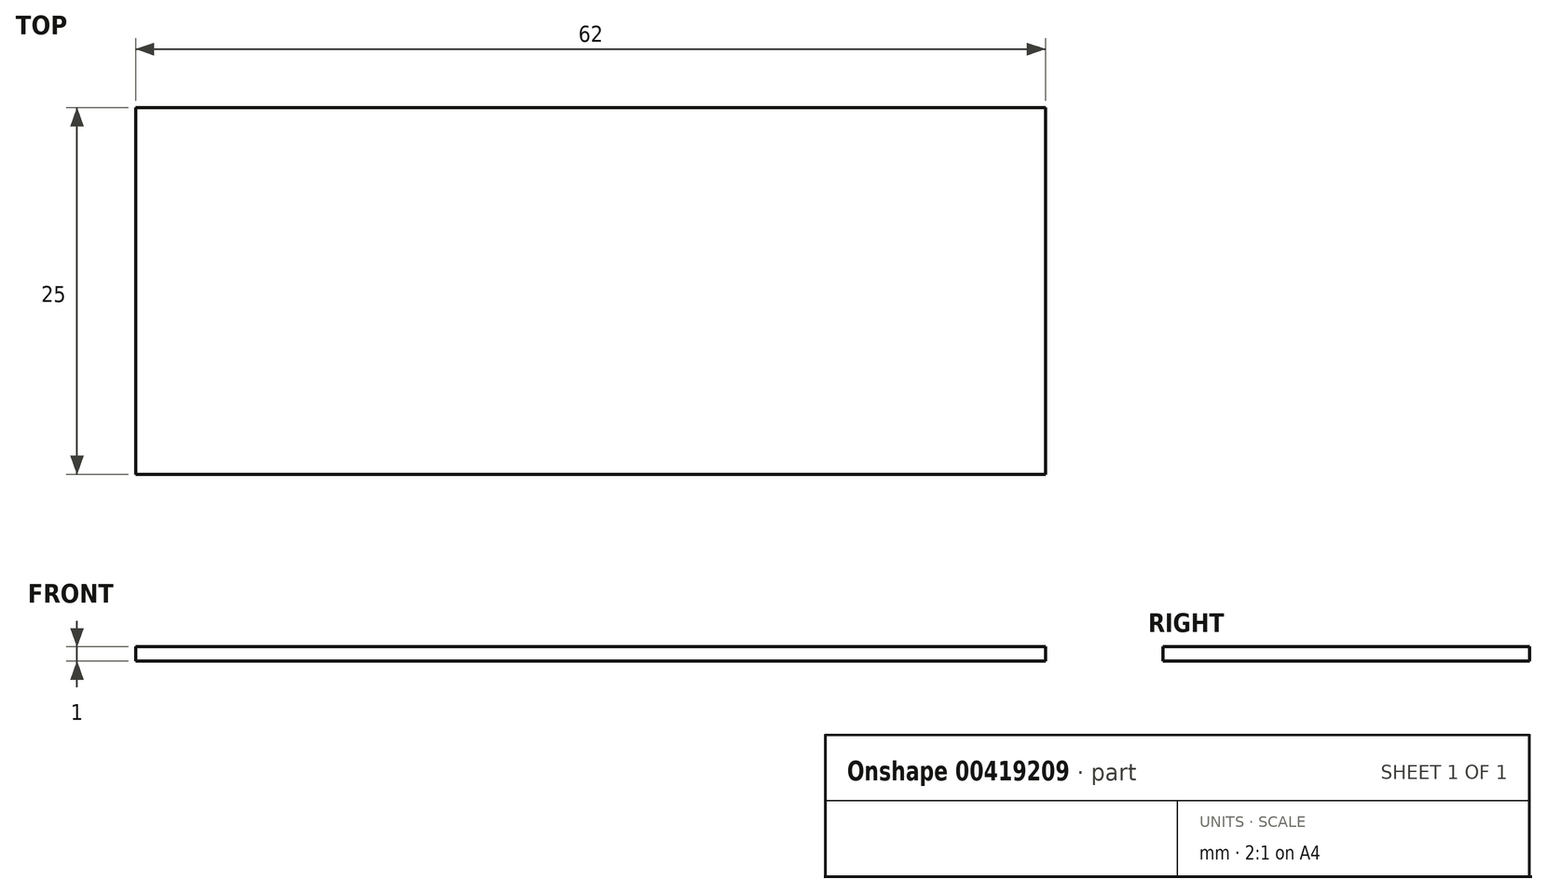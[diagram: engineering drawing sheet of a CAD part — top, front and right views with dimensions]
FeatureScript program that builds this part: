
annotation { "Feature Type Name" : "Feature", "Feature Type Description" : "" }
export const myFeature = defineFeature(function(context is Context, id is Id, definition is map)
    precondition{}
    {
        {
            var Q0;
            Q0=qCreatedBy(makeId("Top.planeOp"),FACE);
            var sketch = newSketch(context, id + "F0", { "sketchPlane" : qUnion([Q0])});
            skLineSegment(sketch, "E0.bottom", {"start": v(31, 12.5) * mm, "end": v(-31, 12.5) * mm});
            skLineSegment(sketch, "E0.top", {"start": v(31, -12.5) * mm, "end": v(-31, -12.5) * mm});
            skLineSegment(sketch, "E0.left", {"start": v(31, 12.5) * mm, "end": v(31, -12.5) * mm});
            skLineSegment(sketch, "E0.right", {"start": v(-31, 12.5) * mm, "end": v(-31, -12.5) * mm});
            skPoint(sketch, "E0.middle", {"position": v(0, 0) * mm});
            skSolve(sketch);
        }
        {
            var Q0;
            Q0=makeQuery(id+"F0.imprint","IMPRINT",FACE,{"disambiguationData":[TD([[makeQuery(id+"F0.imprint","IMPRINT",EDGE,{"derivedFrom":sQuery(id+"F0.wireOp",EDGE,"E0.bottom")}),1.0]])]});
            extrude(context, id + "F1", {"entities" : qUnion([Q0]), "depth" : 1 * mm});
        }
    });
